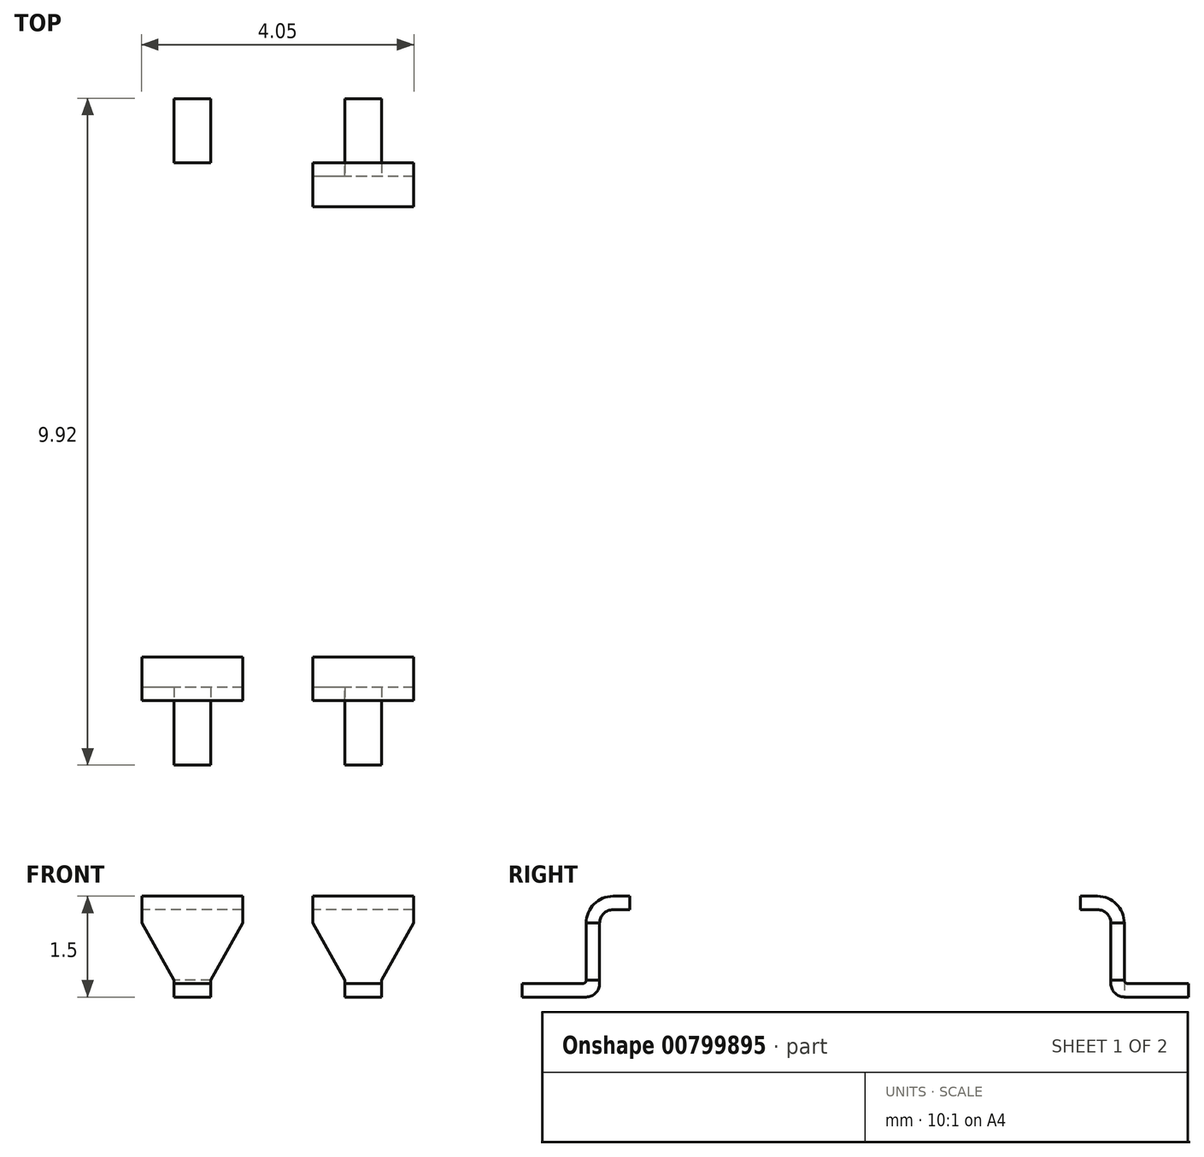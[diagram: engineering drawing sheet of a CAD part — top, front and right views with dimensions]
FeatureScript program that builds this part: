
annotation { "Feature Type Name" : "Feature", "Feature Type Description" : "" }
export const myFeature = defineFeature(function(context is Context, id is Id, definition is map)
    precondition{}
    {
        {
            var Q0;
            Q0=qCreatedBy(makeId("Top.planeOp"),FACE);
            var sketch = newSketch(context, id + "F0", { "sketchPlane" : qUnion([Q0])});
            skLineSegment(sketch, "E0.bottom", {"start": v(0, 3.35) * mm, "end": v(6.55, 3.35) * mm});
            skLineSegment(sketch, "E0.top", {"start": v(0, -3.35) * mm, "end": v(6.55, -3.35) * mm});
            skLineSegment(sketch, "E0.left", {"start": v(0, 3.35) * mm, "end": v(0, -3.35) * mm});
            skLineSegment(sketch, "E0.right", {"start": v(6.55, 3.35) * mm, "end": v(6.55, -3.35) * mm});
            skLineSegment(sketch, "E1.bottom", {"start": v(1.5, 1.81) * mm, "end": v(2.5, 1.81) * mm});
            skLineSegment(sketch, "E1.top", {"start": v(1.5, -1.81) * mm, "end": v(2.5, -1.81) * mm});
            skLineSegment(sketch, "E2.bottom", {"start": v(4.04, 1.81) * mm, "end": v(5.04, 1.81) * mm});
            skLineSegment(sketch, "E2.top", {"start": v(4.04, -1.81) * mm, "end": v(5.04, -1.81) * mm});
            skLineSegment(sketch, "E3", {"start": v(2, 2.56) * mm, "end": v(2, -2.44) * mm, "construction": true});
            skLineSegment(sketch, "E4", {"start": v(4.55, 2.56) * mm, "end": v(4.55, -2.44) * mm, "construction": true});
            skLineSegment(sketch, "E5", {"start": v(3.27, 6.03) * mm, "end": v(3.28, -6.01) * mm, "construction": true});
            skLineSegment(sketch, "E6.bottom", {"start": v(1.6, 0.81) * mm, "end": v(2.4, 0.81) * mm});
            skLineSegment(sketch, "E6.top", {"start": v(1.6, -0.19) * mm, "end": v(2.4, -0.19) * mm});
            skLineSegment(sketch, "E6.left", {"start": v(1.5, 0.71) * mm, "end": v(1.5, -0.09) * mm});
            skLineSegment(sketch, "E6.right", {"start": v(2.5, 0.71) * mm, "end": v(2.5, -0.09) * mm});
            skLineSegment(sketch, "E7.bottom", {"start": v(4.15, 0.81) * mm, "end": v(4.94, 0.81) * mm});
            skLineSegment(sketch, "E7.top", {"start": v(4.15, -0.19) * mm, "end": v(4.94, -0.19) * mm});
            skLineSegment(sketch, "E7.left", {"start": v(4.04, 0.71) * mm, "end": v(4.04, -0.09) * mm});
            skLineSegment(sketch, "E7.right", {"start": v(5.04, 0.71) * mm, "end": v(5.04, -0.09) * mm});
            skPoint(sketch, "E8.visualSharp", {"position": v(1.5, 0.81) * mm});
            skArc(sketch, "E8.filletArc", {"start": v(1.6, 0.81) * mm, "mid": v(1.53, 0.78) * mm, "end": v(1.5, 0.71) * mm});
            skPoint(sketch, "E9.visualSharp", {"position": v(2.5, 0.81) * mm});
            skArc(sketch, "E9.filletArc", {"start": v(2.5, 0.71) * mm, "mid": v(2.48, 0.78) * mm, "end": v(2.4, 0.8) * mm});
            skPoint(sketch, "E10.visualSharp", {"position": v(2.5, -0.19) * mm});
            skArc(sketch, "E10.filletArc", {"start": v(2.4, -0.19) * mm, "mid": v(2.48, -0.16) * mm, "end": v(2.5, -0.09) * mm});
            skPoint(sketch, "E11.visualSharp", {"position": v(1.5, -0.19) * mm});
            skArc(sketch, "E11.filletArc", {"start": v(1.5, -0.09) * mm, "mid": v(1.53, -0.16) * mm, "end": v(1.6, -0.19) * mm});
            skPoint(sketch, "E12.visualSharp", {"position": v(4.04, 0.81) * mm});
            skArc(sketch, "E12.filletArc", {"start": v(4.15, 0.81) * mm, "mid": v(4.07, 0.78) * mm, "end": v(4.04, 0.71) * mm});
            skPoint(sketch, "E13.visualSharp", {"position": v(4.04, -0.19) * mm});
            skArc(sketch, "E13.filletArc", {"start": v(4.04, -0.09) * mm, "mid": v(4.07, -0.16) * mm, "end": v(4.15, -0.19) * mm});
            skPoint(sketch, "E14.visualSharp", {"position": v(5.04, -0.19) * mm});
            skArc(sketch, "E14.filletArc", {"start": v(4.94, -0.19) * mm, "mid": v(5.02, -0.16) * mm, "end": v(5.04, -0.09) * mm});
            skPoint(sketch, "E15.visualSharp", {"position": v(5.04, 0.81) * mm});
            skArc(sketch, "E15.filletArc", {"start": v(5.04, 0.71) * mm, "mid": v(5.02, 0.78) * mm, "end": v(4.94, 0.81) * mm});
            skLineSegment(sketch, "E16", {"start": v(1.5, 1.81) * mm, "end": v(1.5, -1.81) * mm});
            skLineSegment(sketch, "E17", {"start": v(2.5, 1.81) * mm, "end": v(2.5, -1.81) * mm});
            skLineSegment(sketch, "E18", {"start": v(4.05, 1.8) * mm, "end": v(4.05, -1.8) * mm});
            skLineSegment(sketch, "E19", {"start": v(5.04, 1.8) * mm, "end": v(5.05, -1.8) * mm});
            skLineSegment(sketch, "E20", {"start": v(1.5, 0.81) * mm, "end": v(2.5, 0.81) * mm});
            skLineSegment(sketch, "E21", {"start": v(1.5, -0.19) * mm, "end": v(2.5, -0.19) * mm});
            skLineSegment(sketch, "E22", {"start": v(4.04, 0.81) * mm, "end": v(5.04, 0.81) * mm});
            skLineSegment(sketch, "E23", {"start": v(4.04, -0.19) * mm, "end": v(5.04, -0.19) * mm});
            skLineSegment(sketch, "E24", {"start": v(0, -2.35) * mm, "end": v(1, -3.35) * mm});
            skLineSegment(sketch, "E25", {"start": v(5.55, 3.35) * mm, "end": v(6.55, 2.35) * mm});
            skSolve(sketch);
        }
        {
            var Q0;
            {var subQ3=sQuery(id+"F0.wireOp",EDGE,"E24");Q0=makeQuery(id+"F0.imprint","IMPRINT",FACE,{"disambiguationData":[TD([[makeQuery(id+"F0.imprint","IMPRINT",EDGE,{"derivedFrom":subQ3}),-1.0]])]});}
            var Q1;
            {var subQ3=sQuery(id+"F0.wireOp",EDGE,"E25");Q1=makeQuery(id+"F0.imprint","IMPRINT",FACE,{"disambiguationData":[TD([[makeQuery(id+"F0.imprint","IMPRINT",EDGE,{"derivedFrom":subQ3}),1.0]])]});}
            var Q2;
            {var subQ5=sQuery(id+"F0.wireOp",EDGE,"E1.bottom");Q2=makeQuery(id+"F0.imprint","IMPRINT",FACE,{"disambiguationData":[TD([[makeQuery(id+"F0.imprint","IMPRINT",EDGE,{"derivedFrom":subQ5}),1.0]])]});}
            var Q3;
            {var subQ5=sQuery(id+"F0.wireOp",EDGE,"E2.bottom");Q3=makeQuery(id+"F0.imprint","IMPRINT",FACE,{"disambiguationData":[TD([[makeQuery(id+"F0.imprint","IMPRINT",EDGE,{"derivedFrom":subQ5}),-1.0]])]});}
            var Q4;
            {var subQ5=sQuery(id+"F0.wireOp",EDGE,"E2.top");Q4=makeQuery(id+"F0.imprint","IMPRINT",FACE,{"disambiguationData":[TD([[makeQuery(id+"F0.imprint","IMPRINT",EDGE,{"derivedFrom":subQ5}),1.0]])]});}
            var Q5;
            {var subQ5=sQuery(id+"F0.wireOp",EDGE,"E1.top");Q5=makeQuery(id+"F0.imprint","IMPRINT",FACE,{"disambiguationData":[TD([[makeQuery(id+"F0.imprint","IMPRINT",EDGE,{"derivedFrom":subQ5}),1.0]])]});}
            var Q6;
            {var subQ3=sQuery(id+"F0.wireOp",EDGE,"E8.filletArc");Q6=makeQuery(id+"F0.imprint","IMPRINT",FACE,{"disambiguationData":[TD([[makeQuery(id+"F0.imprint","IMPRINT",EDGE,{"derivedFrom":subQ3}),1.0]])]});}
            var Q7;
            {var subQ5=sQuery(id+"F0.wireOp",EDGE,"E1.bottom");Q7=makeQuery(id+"F0.imprint","IMPRINT",FACE,{"disambiguationData":[TD([[makeQuery(id+"F0.imprint","IMPRINT",EDGE,{"derivedFrom":subQ5}),-1.0]])]});}
            var Q8;
            {var subQ4=sQuery(id+"F0.wireOp",EDGE,"E12.filletArc");Q8=makeQuery(id+"F0.imprint","IMPRINT",FACE,{"disambiguationData":[TD([[makeQuery(id+"F0.imprint","IMPRINT",EDGE,{"derivedFrom":subQ4}),1.0]])]});}
            var Q9;
            {var subQ0=sQuery(id+"F0.wireOp",EDGE,"E8.filletArc");Q9=makeQuery(id+"F0.imprint","IMPRINT",FACE,{"disambiguationData":[TD([[makeQuery(id+"F0.imprint","IMPRINT",EDGE,{"derivedFrom":subQ0}),-1.0]])]});}
            var Q10;
            {var subQ0=sQuery(id+"F0.wireOp",EDGE,"E11.filletArc");Q10=makeQuery(id+"F0.imprint","IMPRINT",FACE,{"disambiguationData":[TD([[makeQuery(id+"F0.imprint","IMPRINT",EDGE,{"derivedFrom":subQ0}),-1.0]])]});}
            var Q11;
            {var subQ0=sQuery(id+"F0.wireOp",EDGE,"E10.filletArc");Q11=makeQuery(id+"F0.imprint","IMPRINT",FACE,{"disambiguationData":[TD([[makeQuery(id+"F0.imprint","IMPRINT",EDGE,{"derivedFrom":subQ0}),-1.0]])]});}
            var Q12;
            {var subQ0=sQuery(id+"F0.wireOp",EDGE,"E9.filletArc");Q12=makeQuery(id+"F0.imprint","IMPRINT",FACE,{"disambiguationData":[TD([[makeQuery(id+"F0.imprint","IMPRINT",EDGE,{"derivedFrom":subQ0}),-1.0]])]});}
            var Q13;
            {var subQ0=sQuery(id+"F0.wireOp",EDGE,"E12.filletArc");Q13=makeQuery(id+"F0.imprint","IMPRINT",FACE,{"disambiguationData":[TD([[makeQuery(id+"F0.imprint","IMPRINT",EDGE,{"derivedFrom":subQ0}),-1.0]])]});}
            var Q14;
            {var subQ0=sQuery(id+"F0.wireOp",EDGE,"E13.filletArc");Q14=makeQuery(id+"F0.imprint","IMPRINT",FACE,{"disambiguationData":[TD([[makeQuery(id+"F0.imprint","IMPRINT",EDGE,{"derivedFrom":subQ0}),-1.0]])]});}
            var Q15;
            {var subQ0=sQuery(id+"F0.wireOp",EDGE,"E14.filletArc");Q15=makeQuery(id+"F0.imprint","IMPRINT",FACE,{"disambiguationData":[TD([[makeQuery(id+"F0.imprint","IMPRINT",EDGE,{"derivedFrom":subQ0}),-1.0]])]});}
            var Q16;
            {var subQ0=sQuery(id+"F0.wireOp",EDGE,"E15.filletArc");Q16=makeQuery(id+"F0.imprint","IMPRINT",FACE,{"disambiguationData":[TD([[makeQuery(id+"F0.imprint","IMPRINT",EDGE,{"derivedFrom":subQ0}),-1.0]])]});}
            extrude(context, id + "F1", {"entities" : qUnion([Q0, Q1, Q2, Q3, Q4, Q5, Q6, Q7, Q8, Q9, Q10, Q11, Q12, Q13, Q14, Q15, Q16]), "oppositeDirection" : true, "depth" : 2.5 * mm, "offsetDistance" : 25 * mm});
        }
        {
            var Q0;
            Q0=makeQuery(id+"F1.opExtrude","CAP_FACE",FACE,{"disambiguationData":[OSD([sQuery(id+"F0.wireOp",EDGE,"E0.bottom"),sQuery(id+"F0.wireOp",EDGE,"E0.top"),sQuery(id+"F0.wireOp",EDGE,"E0.left"),sQuery(id+"F0.wireOp",EDGE,"E0.right")])],"isStart":false});
            extrude(context, id + "F2", {"entities" : qUnion([Q0]), "operationType" : NewBodyOperationType.ADD, "depth" : 1.05 * mm, "offsetDistance" : 25 * mm, "hasDraft" : true, "draftAngle" : 20 * degree, "draftPullDirection" : true});
        }
        {
            var Q0;
            Q0=makeQuery(id+"F0.imprint","IMPRINT",FACE,{"disambiguationData":[TD([[makeQuery(id+"F0.imprint","IMPRINT",EDGE,{"derivedFrom":sQuery(id+"F0.wireOp",EDGE,"E1.bottom")}),-1.0]])]});
            var Q1;
            Q1=makeQuery(id+"F0.imprint","IMPRINT",FACE,{"disambiguationData":[TD([[makeQuery(id+"F0.imprint","IMPRINT",EDGE,{"derivedFrom":sQuery(id+"F0.wireOp",EDGE,"E2.bottom")}),-1.0]])]});
            var Q2;
            {var subQ0=sQuery(id+"F0.wireOp",EDGE,"E1.top");Q2=makeQuery(id+"F0.imprint","IMPRINT",FACE,{"disambiguationData":[TD([[makeQuery(id+"F0.imprint","IMPRINT",EDGE,{"derivedFrom":subQ0}),1.0]])]});}
            var Q3;
            {var subQ0=sQuery(id+"F0.wireOp",EDGE,"E2.top");Q3=makeQuery(id+"F0.imprint","IMPRINT",FACE,{"disambiguationData":[TD([[makeQuery(id+"F0.imprint","IMPRINT",EDGE,{"derivedFrom":subQ0}),1.0]])]});}
            var Q4;
            {var subQ0=sQuery(id+"F0.wireOp",EDGE,"E8.filletArc");Q4=makeQuery(id+"F0.imprint","IMPRINT",FACE,{"disambiguationData":[TD([[makeQuery(id+"F0.imprint","IMPRINT",EDGE,{"derivedFrom":subQ0}),-1.0]])]});}
            var Q5;
            {var subQ0=sQuery(id+"F0.wireOp",EDGE,"E9.filletArc");Q5=makeQuery(id+"F0.imprint","IMPRINT",FACE,{"disambiguationData":[TD([[makeQuery(id+"F0.imprint","IMPRINT",EDGE,{"derivedFrom":subQ0}),-1.0]])]});}
            var Q6;
            {var subQ0=sQuery(id+"F0.wireOp",EDGE,"E10.filletArc");Q6=makeQuery(id+"F0.imprint","IMPRINT",FACE,{"disambiguationData":[TD([[makeQuery(id+"F0.imprint","IMPRINT",EDGE,{"derivedFrom":subQ0}),-1.0]])]});}
            var Q7;
            {var subQ0=sQuery(id+"F0.wireOp",EDGE,"E11.filletArc");Q7=makeQuery(id+"F0.imprint","IMPRINT",FACE,{"disambiguationData":[TD([[makeQuery(id+"F0.imprint","IMPRINT",EDGE,{"derivedFrom":subQ0}),-1.0]])]});}
            var Q8;
            {var subQ0=sQuery(id+"F0.wireOp",EDGE,"E12.filletArc");Q8=makeQuery(id+"F0.imprint","IMPRINT",FACE,{"disambiguationData":[TD([[makeQuery(id+"F0.imprint","IMPRINT",EDGE,{"derivedFrom":subQ0}),-1.0]])]});}
            var Q9;
            {var subQ0=sQuery(id+"F0.wireOp",EDGE,"E15.filletArc");Q9=makeQuery(id+"F0.imprint","IMPRINT",FACE,{"disambiguationData":[TD([[makeQuery(id+"F0.imprint","IMPRINT",EDGE,{"derivedFrom":subQ0}),-1.0]])]});}
            var Q10;
            {var subQ0=sQuery(id+"F0.wireOp",EDGE,"E14.filletArc");Q10=makeQuery(id+"F0.imprint","IMPRINT",FACE,{"disambiguationData":[TD([[makeQuery(id+"F0.imprint","IMPRINT",EDGE,{"derivedFrom":subQ0}),-1.0]])]});}
            var Q11;
            {var subQ0=sQuery(id+"F0.wireOp",EDGE,"E13.filletArc");Q11=makeQuery(id+"F0.imprint","IMPRINT",FACE,{"disambiguationData":[TD([[makeQuery(id+"F0.imprint","IMPRINT",EDGE,{"derivedFrom":subQ0}),-1.0]])]});}
            var Q12;
            {var subQ3=sQuery(id+"F0.wireOp",EDGE,"E8.filletArc");Q12=makeQuery(id+"F0.imprint","IMPRINT",FACE,{"disambiguationData":[TD([[makeQuery(id+"F0.imprint","IMPRINT",EDGE,{"derivedFrom":subQ3}),1.0]])]});}
            var Q13;
            {var subQ4=sQuery(id+"F0.wireOp",EDGE,"E12.filletArc");Q13=makeQuery(id+"F0.imprint","IMPRINT",FACE,{"disambiguationData":[TD([[makeQuery(id+"F0.imprint","IMPRINT",EDGE,{"derivedFrom":subQ4}),1.0]])]});}
            extrude(context, id + "F3", {"entities" : qUnion([Q0, Q1, Q2, Q3, Q4, Q5, Q6, Q7, Q8, Q9, Q10, Q11, Q12, Q13]), "operationType" : NewBodyOperationType.REMOVE, "oppositeDirection" : true, "depth" : 0.5 * mm, "offsetDistance" : 25 * mm});
        }
        {
            var Q0;
            {var subQ3=sQuery(id+"F0.wireOp",EDGE,"E8.filletArc");Q0=makeQuery(id+"F0.imprint","IMPRINT",FACE,{"disambiguationData":[TD([[makeQuery(id+"F0.imprint","IMPRINT",EDGE,{"derivedFrom":subQ3}),1.0]])]});}
            var Q1;
            {var subQ4=sQuery(id+"F0.wireOp",EDGE,"E12.filletArc");Q1=makeQuery(id+"F0.imprint","IMPRINT",FACE,{"disambiguationData":[TD([[makeQuery(id+"F0.imprint","IMPRINT",EDGE,{"derivedFrom":subQ4}),1.0]])]});}
            extrude(context, id + "F4", {"entities" : qUnion([Q0, Q1]), "depth" : 0.25 * mm, "offsetDistance" : 25 * mm, "hasSecondDirection" : true, "secondDirectionOppositeDirection" : true, "secondDirectionDepth" : 0.5 * mm});
        }
        {
            var Q0;
            Q0=makeQuery(id+"F4.opExtrude","CAP_FACE",FACE,{"disambiguationData":[OSD([sQuery(id+"F0.wireOp",EDGE,"E8.filletArc"),sQuery(id+"F0.wireOp",EDGE,"E9.filletArc"),sQuery(id+"F0.wireOp",EDGE,"E10.filletArc"),sQuery(id+"F0.wireOp",EDGE,"E11.filletArc"),sQuery(id+"F0.wireOp",EDGE,"E16"),sQuery(id+"F0.wireOp",EDGE,"E17"),sQuery(id+"F0.wireOp",EDGE,"E20"),sQuery(id+"F0.wireOp",EDGE,"E21")])],"isStart":false});
            var Q1;
            Q1=makeQuery(id+"F4.opExtrude","CAP_FACE",FACE,{"disambiguationData":[OSD([sQuery(id+"F0.wireOp",EDGE,"E12.filletArc"),sQuery(id+"F0.wireOp",EDGE,"E13.filletArc"),sQuery(id+"F0.wireOp",EDGE,"E14.filletArc"),sQuery(id+"F0.wireOp",EDGE,"E15.filletArc"),sQuery(id+"F0.wireOp",EDGE,"E18"),sQuery(id+"F0.wireOp",EDGE,"E19"),sQuery(id+"F0.wireOp",EDGE,"E22"),sQuery(id+"F0.wireOp",EDGE,"E23")])],"isStart":false});
            fillet(context, id + "F5", {"entities" : qUnion([Q0, Q1]), "radius" : 0.05 * mm, "tangentPropagation" : true, "allowEdgeOverflow" : false});
        }
        {
            var Q0;
            {var subQ3=sQuery(id+"F0.wireOp",EDGE,"E24");Q0=makeQuery(id+"F0.imprint","IMPRINT",FACE,{"disambiguationData":[TD([[makeQuery(id+"F0.imprint","IMPRINT",EDGE,{"derivedFrom":subQ3}),-1.0]])]});}
            var Q1;
            {var subQ3=sQuery(id+"F0.wireOp",EDGE,"E25");Q1=makeQuery(id+"F0.imprint","IMPRINT",FACE,{"disambiguationData":[TD([[makeQuery(id+"F0.imprint","IMPRINT",EDGE,{"derivedFrom":subQ3}),1.0]])]});}
            extrude(context, id + "F6", {"entities" : qUnion([Q0, Q1]), "operationType" : NewBodyOperationType.REMOVE, "oppositeDirection" : true, "depth" : 0.5 * mm, "offsetDistance" : 25 * mm});
        }
        {
            var Q0;
            {var subQ0=sQuery(id+"F0.wireOp",EDGE,"E0.bottom");Q0=makeQuery(id+"F2.boolean.opBoolean","MERGE",EDGE,{"derivedFrom":[makeQuery(id+"F1.opExtrude","CAP_EDGE",EDGE,{"disambiguationData":[OSD([subQ0])],"isStart":false}),makeQuery(id+"F2.opExtrude","CAP_EDGE",EDGE,{"disambiguationData":[OSD([subQ0])],"isStart":true})]});}
            var Q1;
            {var subQ0=sQuery(id+"F0.wireOp",EDGE,"E0.left");Q1=makeQuery(id+"F2.boolean.opBoolean","MERGE",EDGE,{"derivedFrom":[makeQuery(id+"F1.opExtrude","CAP_EDGE",EDGE,{"disambiguationData":[OSD([subQ0])],"isStart":false}),makeQuery(id+"F2.opExtrude","CAP_EDGE",EDGE,{"disambiguationData":[OSD([subQ0])],"isStart":true})]});}
            cPlane(context, id + "F7", {"entities" : qUnion([Q0, Q1]), "cplaneType" : CPlaneType.LINE_ANGLE, "offset" : 25 * mm, "angle" : 0 * degree, "width" : 150 * mm, "height" : 150 * mm});
        }
        {
            var Q0;
            Q0=qCreatedBy(id+"F7.planeOp",FACE);
            var sketch = newSketch(context, id + "F8", { "sketchPlane" : qUnion([Q0])});
            skLineSegment(sketch, "E26.0", {"start": v(2, -2.56) * mm, "end": v(2, 2.44) * mm});
            skLineSegment(sketch, "E27.0", {"start": v(4.55, -2.56) * mm, "end": v(4.55, 2.44) * mm});
            skLineSegment(sketch, "E28.0", {"start": v(0, -3.35) * mm, "end": v(6.55, -3.35) * mm});
            skLineSegment(sketch, "E29.0", {"start": v(0, 3.35) * mm, "end": v(6.55, 3.35) * mm});
            skLineSegment(sketch, "E30.bottom", {"start": v(1.26, -4) * mm, "end": v(2.75, -4) * mm});
            skLineSegment(sketch, "E30.top", {"start": v(1.25, -3.35) * mm, "end": v(2.76, -3.35) * mm});
            skLineSegment(sketch, "E30.left", {"start": v(1.25, -4) * mm, "end": v(1.25, -3.35) * mm});
            skLineSegment(sketch, "E30.right", {"start": v(2.75, -4) * mm, "end": v(2.75, -3.35) * mm});
            skLineSegment(sketch, "E31.bottom", {"start": v(1.73, -4.96) * mm, "end": v(2.28, -4.96) * mm});
            skLineSegment(sketch, "E31.top", {"start": v(1.73, -4) * mm, "end": v(2.28, -4) * mm});
            skLineSegment(sketch, "E31.left", {"start": v(1.73, -4.96) * mm, "end": v(1.73, -4) * mm});
            skLineSegment(sketch, "E31.right", {"start": v(2.28, -4.96) * mm, "end": v(2.28, -4) * mm});
            skLineSegment(sketch, "E32.MirrorCS", {"start": v(4.82, -4.96) * mm, "end": v(4.27, -4.96) * mm});
            skLineSegment(sketch, "E33.MirrorCS", {"start": v(4.82, -4.96) * mm, "end": v(4.82, -4) * mm});
            skLineSegment(sketch, "E34.MirrorCS", {"start": v(5.3, -4) * mm, "end": v(3.8, -4) * mm});
            skLineSegment(sketch, "E35.MirrorCS", {"start": v(5.3, -4) * mm, "end": v(5.3, -3.35) * mm});
            skLineSegment(sketch, "E36.MirrorCS", {"start": v(3.8, -4) * mm, "end": v(3.8, -3.35) * mm});
            skLineSegment(sketch, "E37.MirrorCS", {"start": v(4.27, -4.96) * mm, "end": v(4.27, -4) * mm});
            skLineSegment(sketch, "E38", {"start": v(-1.83, 0) * mm, "end": v(9.08, 0) * mm, "construction": true});
            skLineSegment(sketch, "E39.MirrorCS", {"start": v(1.25, 4) * mm, "end": v(1.25, 3.35) * mm});
            skLineSegment(sketch, "E40.MirrorCS", {"start": v(1.26, 4) * mm, "end": v(2.75, 4) * mm});
            skLineSegment(sketch, "E41.MirrorCS", {"start": v(1.73, 4.96) * mm, "end": v(1.73, 4) * mm});
            skLineSegment(sketch, "E42.MirrorCS", {"start": v(1.73, 4.96) * mm, "end": v(2.28, 4.96) * mm});
            skLineSegment(sketch, "E43.MirrorCS", {"start": v(2.28, 4.96) * mm, "end": v(2.28, 4) * mm});
            skLineSegment(sketch, "E44.MirrorCS", {"start": v(2.75, 4) * mm, "end": v(2.75, 3.35) * mm});
            skLineSegment(sketch, "E45.MirrorCS", {"start": v(3.8, 4) * mm, "end": v(3.8, 3.35) * mm});
            skLineSegment(sketch, "E46.MirrorCS", {"start": v(5.3, 4) * mm, "end": v(3.8, 4) * mm});
            skLineSegment(sketch, "E47.MirrorCS", {"start": v(4.27, 4.96) * mm, "end": v(4.27, 4) * mm});
            skLineSegment(sketch, "E48.MirrorCS", {"start": v(4.82, 4.96) * mm, "end": v(4.27, 4.96) * mm});
            skLineSegment(sketch, "E49.MirrorCS", {"start": v(4.82, 4.96) * mm, "end": v(4.82, 4) * mm});
            skLineSegment(sketch, "E50.MirrorCS", {"start": v(5.3, 4) * mm, "end": v(5.3, 3.35) * mm});
            skSolve(sketch);
        }
        {
            var Q0;
            Q0=makeQuery(id+"F8.imprint","IMPRINT",FACE,{"disambiguationData":[TD([[makeQuery(id+"F8.imprint","IMPRINT",EDGE,{"derivedFrom":sQuery(id+"F8.wireOp",EDGE,"E31.bottom")}),1.0]])]});
            var Q1;
            Q1=makeQuery(id+"F8.imprint","IMPRINT",FACE,{"disambiguationData":[TD([[makeQuery(id+"F8.imprint","IMPRINT",EDGE,{"derivedFrom":sQuery(id+"F8.wireOp",EDGE,"E30.top")}),-1.0]])]});
            var Q2;
            {var subQ4=sQuery(id+"F8.wireOp",EDGE,"E35.MirrorCS");Q2=makeQuery(id+"F8.imprint","IMPRINT",FACE,{"disambiguationData":[TD([[makeQuery(id+"F8.imprint","IMPRINT",EDGE,{"derivedFrom":subQ4}),1.0]])]});}
            var Q3;
            Q3=makeQuery(id+"F8.imprint","IMPRINT",FACE,{"disambiguationData":[TD([[makeQuery(id+"F8.imprint","IMPRINT",EDGE,{"derivedFrom":sQuery(id+"F8.wireOp",EDGE,"E32.MirrorCS")}),-1.0]])]});
            var Q4;
            {var subQ3=sQuery(id+"F8.wireOp",EDGE,"E39.MirrorCS");Q4=makeQuery(id+"F8.imprint","IMPRINT",FACE,{"disambiguationData":[TD([[makeQuery(id+"F8.imprint","IMPRINT",EDGE,{"derivedFrom":subQ3}),1.0]])]});}
            var Q5;
            {var subQ0=sQuery(id+"F8.wireOp",EDGE,"E41.MirrorCS");Q5=makeQuery(id+"F8.imprint","IMPRINT",FACE,{"disambiguationData":[TD([[makeQuery(id+"F8.imprint","IMPRINT",EDGE,{"derivedFrom":subQ0}),1.0]])]});}
            var Q6;
            {var subQ3=sQuery(id+"F8.wireOp",EDGE,"E45.MirrorCS");Q6=makeQuery(id+"F8.imprint","IMPRINT",FACE,{"disambiguationData":[TD([[makeQuery(id+"F8.imprint","IMPRINT",EDGE,{"derivedFrom":subQ3}),1.0]])]});}
            var Q7;
            {var subQ0=sQuery(id+"F8.wireOp",EDGE,"E47.MirrorCS");Q7=makeQuery(id+"F8.imprint","IMPRINT",FACE,{"disambiguationData":[TD([[makeQuery(id+"F8.imprint","IMPRINT",EDGE,{"derivedFrom":subQ0}),1.0]])]});}
            extrude(context, id + "F9", {"entities" : qUnion([Q0, Q1, Q2, Q3, Q4, Q5, Q6, Q7]), "oppositeDirection" : true, "depth" : 0.2 * mm, "offsetDistance" : 25 * mm, "hasSecondDirection" : true, "secondDirectionOppositeDirection" : false, "secondDirectionDepth" : 1.3 * mm});
        }
        {
            var Q0;
            Q0=makeQuery(id+"F1.opExtrude","SWEPT_FACE",FACE,{"disambiguationData":[OSD([sQuery(id+"F0.wireOp",EDGE,"E0.left")])]});
            var sketch = newSketch(context, id + "F10", { "sketchPlane" : qUnion([Q0])});
            skLineSegment(sketch, "E51", {"start": v(-3.35, -2.3) * mm, "end": v(-3.6, -2.3) * mm});
            skLineSegment(sketch, "E52", {"start": v(-4, -2.7) * mm, "end": v(-4, -3.55) * mm});
            skLineSegment(sketch, "E53", {"start": v(-4.05, -3.6) * mm, "end": v(-4.96, -3.6) * mm});
            skLineSegment(sketch, "E54", {"start": v(-4.96, -3.6) * mm, "end": v(-4.96, -3.8) * mm});
            skLineSegment(sketch, "E55", {"start": v(-4.96, -3.8) * mm, "end": v(-4, -3.8) * mm});
            skLineSegment(sketch, "E56", {"start": v(-3.8, -3.6) * mm, "end": v(-3.8, -2.7) * mm});
            skLineSegment(sketch, "E57", {"start": v(-3.6, -2.5) * mm, "end": v(-3.35, -2.5) * mm});
            skPoint(sketch, "E58.visualSharp", {"position": v(-4, -2.3) * mm});
            skArc(sketch, "E58.filletArc", {"start": v(-3.6, -2.3) * mm, "mid": v(-3.88, -2.42) * mm, "end": v(-4, -2.7) * mm});
            skPoint(sketch, "E59.visualSharp", {"position": v(-3.8, -2.5) * mm});
            skArc(sketch, "E59.filletArc", {"start": v(-3.6, -2.5) * mm, "mid": v(-3.74, -2.56) * mm, "end": v(-3.8, -2.7) * mm});
            skPoint(sketch, "E60.visualSharp", {"position": v(-4, -3.6) * mm});
            skArc(sketch, "E60.filletArc", {"start": v(-4.05, -3.6) * mm, "mid": v(-4.01, -3.59) * mm, "end": v(-4, -3.55) * mm});
            skPoint(sketch, "E61.visualSharp", {"position": v(-3.8, -3.8) * mm});
            skArc(sketch, "E61.filletArc", {"start": v(-4, -3.8) * mm, "mid": v(-3.86, -3.74) * mm, "end": v(-3.8, -3.6) * mm});
            skLineSegment(sketch, "E62", {"start": v(0, 0) * mm, "end": v(0, -4.22) * mm, "construction": true});
            skPoint(sketch, "E62.endSnap0", {"position": v(0, -2.5) * mm});
            skLineSegment(sketch, "E63.MirrorCS", {"start": v(3.35, -2.3) * mm, "end": v(3.6, -2.3) * mm});
            skArc(sketch, "E64.MirrorCS", {"start": v(3.6, -2.3) * mm, "mid": v(3.88, -2.42) * mm, "end": v(4, -2.7) * mm});
            skLineSegment(sketch, "E65.MirrorCS", {"start": v(4, -2.7) * mm, "end": v(4, -3.55) * mm});
            skArc(sketch, "E66.MirrorCS", {"start": v(4.05, -3.6) * mm, "mid": v(4.01, -3.59) * mm, "end": v(4, -3.55) * mm});
            skLineSegment(sketch, "E67.MirrorCS", {"start": v(4.05, -3.6) * mm, "end": v(4.96, -3.6) * mm});
            skLineSegment(sketch, "E68.MirrorCS", {"start": v(4.96, -3.6) * mm, "end": v(4.96, -3.8) * mm});
            skLineSegment(sketch, "E69.MirrorCS", {"start": v(4.96, -3.8) * mm, "end": v(4, -3.8) * mm});
            skArc(sketch, "E70.MirrorCS", {"start": v(4, -3.8) * mm, "mid": v(3.86, -3.74) * mm, "end": v(3.8, -3.6) * mm});
            skLineSegment(sketch, "E71.MirrorCS", {"start": v(3.8, -3.6) * mm, "end": v(3.8, -2.7) * mm});
            skArc(sketch, "E72.MirrorCS", {"start": v(3.6, -2.5) * mm, "mid": v(3.74, -2.56) * mm, "end": v(3.8, -2.7) * mm});
            skLineSegment(sketch, "E73.MirrorCS", {"start": v(3.6, -2.5) * mm, "end": v(3.35, -2.5) * mm});
            skSolve(sketch);
        }
        {
            var Q0;
            {var subQ1=sQuery(id+"F10.wireOp",EDGE,"E51");Q0=makeQuery(id+"F10.imprint","IMPRINT",FACE,{"disambiguationData":[TD([[makeQuery(id+"F10.imprint","IMPRINT",EDGE,{"derivedFrom":subQ1}),1.0]])]});}
            var Q1;
            {var subQ0=sQuery(id+"F10.wireOp",EDGE,"E63.MirrorCS");Q1=makeQuery(id+"F10.imprint","IMPRINT",FACE,{"disambiguationData":[TD([[makeQuery(id+"F10.imprint","IMPRINT",EDGE,{"derivedFrom":subQ0}),-1.0]])]});}
            var Q2;
            Q2=makeQuery(id+"F2.opExtrude","CAP_VERTEX",VERTEX,{"disambiguationData":[OSD([sQuery(id+"F0.wireOp",EDGE,"E0.bottom"),sQuery(id+"F0.wireOp",EDGE,"E0.right")])],"isStart":false});
            extrude(context, id + "F11", {"entities" : qUnion([Q0, Q1]), "operationType" : NewBodyOperationType.INTERSECT, "endBound" : BoundingType.UP_TO_VERTEX, "oppositeDirection" : true, "depth" : 25 * mm, "endBoundEntityVertex" : qUnion([Q2]), "offsetDistance" : 25 * mm});
        }
        {
            var Q0;
            {var subQ0=sQuery(id+"F8.wireOp",EDGE,"E40.MirrorCS");Q0=makeQuery(id+"F11.boolean.opBoolean","MERGE",FACE,{"derivedFrom":[makeQuery(id+"F9.opExtrude","SWEPT_FACE",FACE,{"disambiguationData":[OSD([subQ0]),TDD([makeQuery(id+"F8.imprint","IMPRINT",EDGE,{"disambiguationData":[TD([[makeQuery(id+"F8.imprint","INTERSECT",VERTEX,{"derivedFrom":[sQuery(id+"F8.wireOp",EDGE,"E39.MirrorCS"),subQ0]}),-1.0]])],"derivedFrom":subQ0})])]}),makeQuery(id+"F9.opExtrude","SWEPT_FACE",FACE,{"disambiguationData":[OSD([subQ0]),TDD([makeQuery(id+"F8.imprint","IMPRINT",EDGE,{"disambiguationData":[TD([[makeQuery(id+"F8.imprint","INTERSECT",VERTEX,{"derivedFrom":[subQ0,sQuery(id+"F8.wireOp",EDGE,"E44.MirrorCS")]}),1.0]])],"derivedFrom":subQ0})])]}),makeQuery(id+"F11.boolean.toolComplement.opBoolean","COPY",FACE,{"derivedFrom":makeQuery(id+"F11.opExtrude","SWEPT_FACE",FACE,{"disambiguationData":[OSD([sQuery(id+"F10.wireOp",EDGE,"E65.MirrorCS")])]})})]});}
            var sketch = newSketch(context, id + "F12", { "sketchPlane" : qUnion([Q0])});
            skLineSegment(sketch, "E74.0", {"start": v(2.28, -3.55) * mm, "end": v(1.73, -3.55) * mm});
            skLineSegment(sketch, "E75.0", {"start": v(4.82, -3.55) * mm, "end": v(4.27, -3.55) * mm});
            skPoint(sketch, "E76.0", {"position": v(1.26, -2.7) * mm});
            skPoint(sketch, "E76.1", {"position": v(2.75, -2.7) * mm});
            skPoint(sketch, "E77.0", {"position": v(3.8, -2.7) * mm});
            skPoint(sketch, "E77.1", {"position": v(5.3, -2.7) * mm});
            skPoint(sketch, "E78.0", {"position": v(1.73, -3.8) * mm});
            skPoint(sketch, "E79.0", {"position": v(2.28, -3.8) * mm});
            skPoint(sketch, "E80.0", {"position": v(4.27, -3.8) * mm});
            skPoint(sketch, "E81.0", {"position": v(4.82, -3.8) * mm});
            skLineSegment(sketch, "E82", {"start": v(1.73, -3.8) * mm, "end": v(1.73, -3.55) * mm});
            skPoint(sketch, "E83.0", {"position": v(1.26, -2.3) * mm});
            skPoint(sketch, "E84.0", {"position": v(5.3, -2.3) * mm});
            skPoint(sketch, "E85.0", {"position": v(3.8, -2.3) * mm});
            skPoint(sketch, "E86.0", {"position": v(2.76, -2.3) * mm});
            skLineSegment(sketch, "E87", {"start": v(1.73, -3.55) * mm, "end": v(1.26, -2.7) * mm});
            skLineSegment(sketch, "E88", {"start": v(1.26, -2.7) * mm, "end": v(1.26, -2.3) * mm});
            skLineSegment(sketch, "E89", {"start": v(1.26, -2.3) * mm, "end": v(2.76, -2.3) * mm});
            skLineSegment(sketch, "E90", {"start": v(2.76, -2.3) * mm, "end": v(2.75, -2.7) * mm});
            skLineSegment(sketch, "E91", {"start": v(2.75, -2.7) * mm, "end": v(2.28, -3.55) * mm});
            skLineSegment(sketch, "E92", {"start": v(2.28, -3.55) * mm, "end": v(2.28, -3.8) * mm});
            skLineSegment(sketch, "E93", {"start": v(2.28, -3.8) * mm, "end": v(1.73, -3.8) * mm});
            skLineSegment(sketch, "E94", {"start": v(4.82, -3.8) * mm, "end": v(4.27, -3.8) * mm});
            skLineSegment(sketch, "E95", {"start": v(3.8, -2.7) * mm, "end": v(3.8, -2.3) * mm});
            skLineSegment(sketch, "E96", {"start": v(4.27, -3.55) * mm, "end": v(3.8, -2.7) * mm});
            skLineSegment(sketch, "E97", {"start": v(3.8, -2.3) * mm, "end": v(5.3, -2.3) * mm});
            skLineSegment(sketch, "E98", {"start": v(5.3, -2.3) * mm, "end": v(5.3, -2.7) * mm});
            skLineSegment(sketch, "E99", {"start": v(5.3, -2.7) * mm, "end": v(4.82, -3.55) * mm});
            skLineSegment(sketch, "E100", {"start": v(4.82, -3.55) * mm, "end": v(4.82, -3.8) * mm});
            skLineSegment(sketch, "E101", {"start": v(4.27, -3.8) * mm, "end": v(4.27, -3.55) * mm});
            skSolve(sketch);
        }
        {
            var Q0;
            Q0=makeQuery(id+"F12.imprint","IMPRINT",FACE,{"disambiguationData":[TD([[makeQuery(id+"F12.imprint","IMPRINT",EDGE,{"derivedFrom":sQuery(id+"F12.wireOp",EDGE,"E74.0")}),1.0]])]});
            var Q1;
            Q1=makeQuery(id+"F12.imprint","IMPRINT",FACE,{"disambiguationData":[TD([[makeQuery(id+"F12.imprint","IMPRINT",EDGE,{"derivedFrom":sQuery(id+"F12.wireOp",EDGE,"E74.0")}),-1.0]])]});
            var Q2;
            Q2=makeQuery(id+"F12.imprint","IMPRINT",FACE,{"disambiguationData":[TD([[makeQuery(id+"F12.imprint","IMPRINT",EDGE,{"derivedFrom":sQuery(id+"F12.wireOp",EDGE,"E88")}),-1.0]])]});
            var Q3;
            Q3=makeQuery(id+"F12.imprint","IMPRINT",FACE,{"disambiguationData":[TD([[makeQuery(id+"F12.imprint","IMPRINT",EDGE,{"derivedFrom":sQuery(id+"F12.wireOp",EDGE,"E75.0")}),1.0]])]});
            var Q4;
            Q4=makeQuery(id+"F12.imprint","IMPRINT",FACE,{"disambiguationData":[TD([[makeQuery(id+"F12.imprint","IMPRINT",EDGE,{"derivedFrom":sQuery(id+"F12.wireOp",EDGE,"E75.0")}),-1.0]])]});
            extrude(context, id + "F13", {"entities" : qUnion([Q0, Q1, Q2, Q3, Q4]), "operationType" : NewBodyOperationType.INTERSECT, "endBound" : BoundingType.THROUGH_ALL, "oppositeDirection" : true, "depth" : 25 * mm, "offsetDistance" : 25 * mm, "hasSecondDirection" : true, "secondDirectionBound" : SecondDirectionBoundingType.THROUGH_ALL, "secondDirectionOppositeDirection" : false, "secondDirectionDepth" : 25 * mm});
        }
    });
